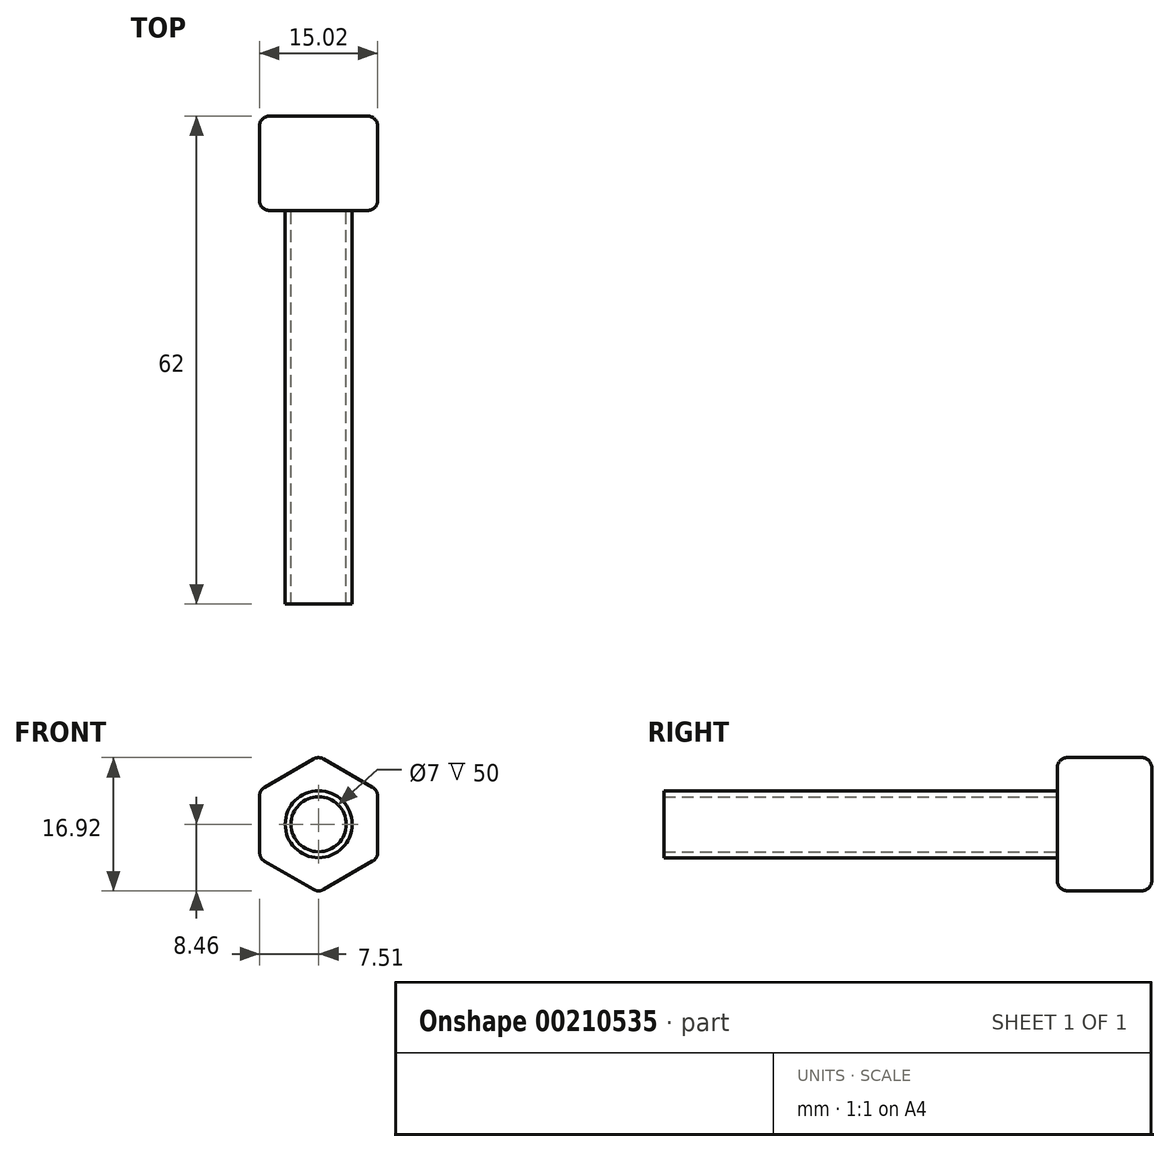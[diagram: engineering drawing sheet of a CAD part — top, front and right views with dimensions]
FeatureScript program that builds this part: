
annotation { "Feature Type Name" : "Feature", "Feature Type Description" : "" }
export const myFeature = defineFeature(function(context is Context, id is Id, definition is map)
    precondition{}
    {
        {
            var Q0;
            Q0=qCreatedBy(makeId("Front.planeOp"),FACE);
            var sketch = newSketch(context, id + "F0", { "sketchPlane" : qUnion([Q0])});
            skCircle(sketch, "E0.cCircle", {"center": v(0, 0) * mm, "radius": 7.5 * mm, "construction": true});
            skLineSegment(sketch, "E0.0", {"start": v(7.5, -4.32) * mm, "end": v(0.02, -8.66) * mm});
            skLineSegment(sketch, "E0.1", {"start": v(0.02, -8.66) * mm, "end": v(-7.5, -4.34) * mm});
            skLineSegment(sketch, "E0.2", {"start": v(-7.5, -4.34) * mm, "end": v(-7.5, 4.32) * mm});
            skLineSegment(sketch, "E0.3", {"start": v(-7.5, 4.32) * mm, "end": v(-0.02, 8.66) * mm});
            skLineSegment(sketch, "E0.4", {"start": v(-0.02, 8.66) * mm, "end": v(7.5, 4.34) * mm});
            skLineSegment(sketch, "E0.5", {"start": v(7.5, 4.34) * mm, "end": v(7.5, -4.32) * mm});
            skPoint(sketch, "E0.0.midPoint", {"position": v(3.76, -6.49) * mm});
            skSolve(sketch);
        }
        {
            var Q0;
            Q0=makeQuery(id+"F0.imprint","IMPRINT",FACE,{"disambiguationData":[TD([[makeQuery(id+"F0.imprint","IMPRINT",EDGE,{"derivedFrom":sQuery(id+"F0.wireOp",EDGE,"E0.0")}),-1.0]])]});
            extrude(context, id + "F1", {"entities" : qUnion([Q0]), "depth" : 12 * mm});
        }
        {
            var Q0;
            Q0=makeQuery(id+"F1.opExtrude","CAP_FACE",FACE,{"disambiguationData":[OSD([sQuery(id+"F0.wireOp",EDGE,"E0.0"),sQuery(id+"F0.wireOp",EDGE,"E0.1"),sQuery(id+"F0.wireOp",EDGE,"E0.2"),sQuery(id+"F0.wireOp",EDGE,"E0.3"),sQuery(id+"F0.wireOp",EDGE,"E0.4"),sQuery(id+"F0.wireOp",EDGE,"E0.5")])],"isStart":false});
            var sketch = newSketch(context, id + "F2", { "sketchPlane" : qUnion([Q0])});
            skCircle(sketch, "E1", {"center": v(0, 0) * mm, "radius": 4.25 * mm});
            skCircle(sketch, "E2", {"center": v(0, 0) * mm, "radius": 3.5 * mm});
            skSolve(sketch);
        }
        {
            var Q0;
            Q0=makeQuery(id+"F2.imprint","IMPRINT",FACE,{"disambiguationData":[TD([[makeQuery(id+"F2.imprint","IMPRINT",EDGE,{"derivedFrom":sQuery(id+"F2.wireOp",EDGE,"E1")}),1.0]])]});
            extrude(context, id + "F3", {"entities" : qUnion([Q0]), "operationType" : NewBodyOperationType.ADD, "depth" : 50 * mm});
        }
        {
            var Q0;
            Q0=makeQuery(id+"F1.opExtrude","SWEPT_FACE",FACE,{"disambiguationData":[OSD([sQuery(id+"F0.wireOp",EDGE,"E0.4")])]});
            var Q1;
            Q1=makeQuery(id+"F1.opExtrude","SWEPT_FACE",FACE,{"disambiguationData":[OSD([sQuery(id+"F0.wireOp",EDGE,"E0.5")])]});
            var Q2;
            Q2=makeQuery(id+"F1.opExtrude","SWEPT_FACE",FACE,{"disambiguationData":[OSD([sQuery(id+"F0.wireOp",EDGE,"E0.3")])]});
            var Q3;
            Q3=makeQuery(id+"F1.opExtrude","SWEPT_FACE",FACE,{"disambiguationData":[OSD([sQuery(id+"F0.wireOp",EDGE,"E0.2")])]});
            var Q4;
            Q4=makeQuery(id+"F1.opExtrude","SWEPT_FACE",FACE,{"disambiguationData":[OSD([sQuery(id+"F0.wireOp",EDGE,"E0.1")])]});
            var Q5;
            Q5=makeQuery(id+"F1.opExtrude","SWEPT_FACE",FACE,{"disambiguationData":[OSD([sQuery(id+"F0.wireOp",EDGE,"E0.0")])]});
            fillet(context, id + "F4", {"entities" : qUnion([Q0, Q1, Q2, Q3, Q4, Q5]), "radius" : 1.27 * mm, "tangentPropagation" : true, "allowEdgeOverflow" : false});
        }
    });
